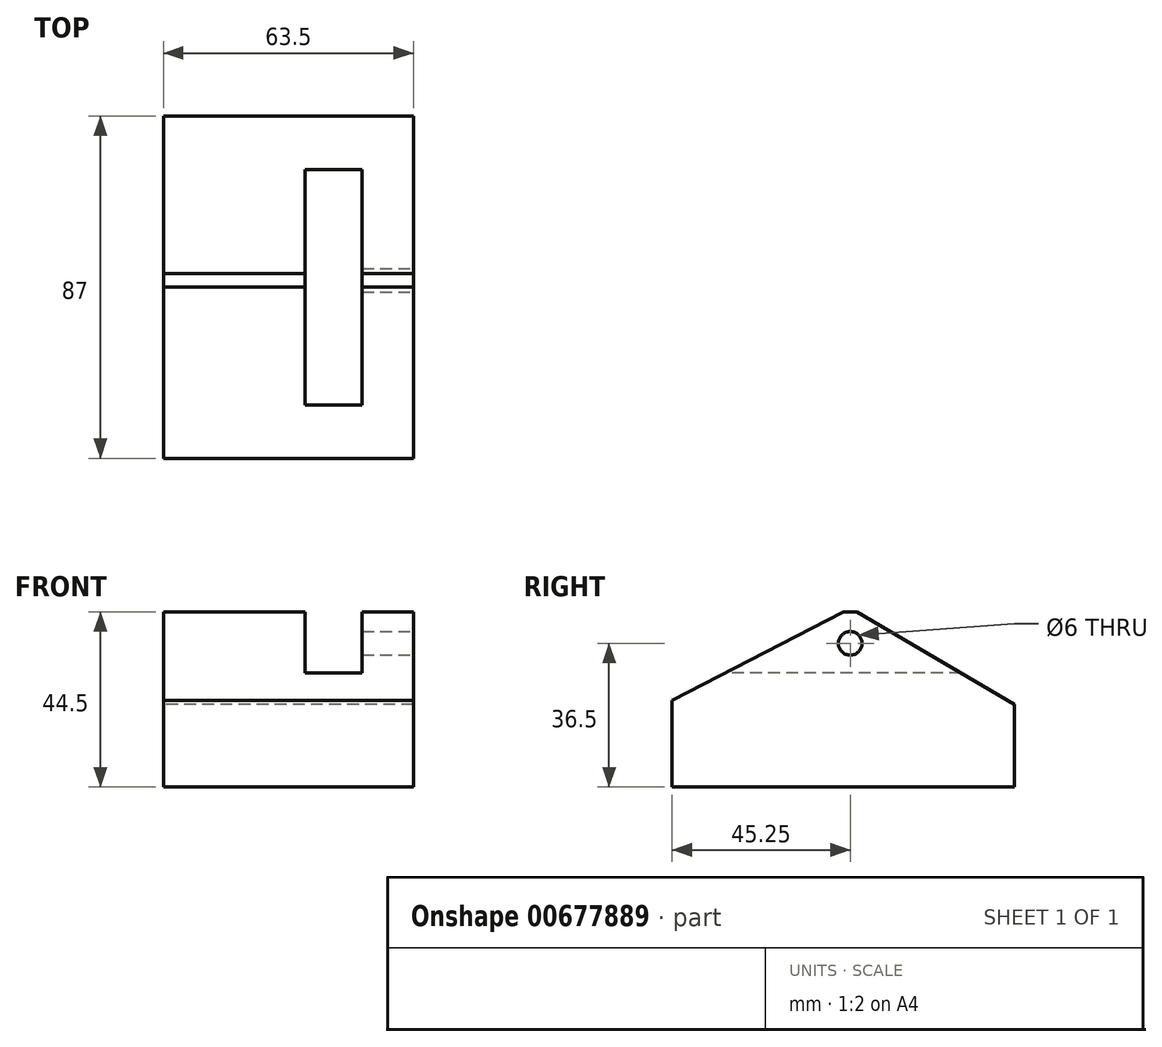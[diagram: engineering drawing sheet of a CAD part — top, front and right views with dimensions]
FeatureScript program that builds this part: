
annotation { "Feature Type Name" : "Feature", "Feature Type Description" : "" }
export const myFeature = defineFeature(function(context is Context, id is Id, definition is map)
    precondition{}
    {
        {
            var Q0;
            Q0=qCreatedBy(makeId("Right.planeOp"),FACE);
            var sketch = newSketch(context, id + "F0", { "sketchPlane" : qUnion([Q0])});
            skLineSegment(sketch, "E0", {"start": v(0, 0) * mm, "end": v(0, 22) * mm});
            skLineSegment(sketch, "E1", {"start": v(0, 22) * mm, "end": v(43.5, 44.5) * mm});
            skLineSegment(sketch, "E2", {"start": v(43.5, 44.5) * mm, "end": v(47, 44.5) * mm});
            skLineSegment(sketch, "E3", {"start": v(47, 44.5) * mm, "end": v(87, 21) * mm});
            skLineSegment(sketch, "E4", {"start": v(87, 21) * mm, "end": v(87, 0) * mm});
            skLineSegment(sketch, "E5", {"start": v(87, 0) * mm, "end": v(0, 0) * mm});
            skSolve(sketch);
        }
        {
            var Q0;
            Q0 = qSketchRegion(id + "F0", true);
            extrude(context, id + "F1", {"entities" : qUnion([Q0]), "depth" : 63.5 * mm, "offsetDistance" : 25 * mm});
        }
        {
            var Q0;
            Q0=makeQuery(id+"F1.opExtrude","SWEPT_FACE",FACE,{"disambiguationData":[OSD([sQuery(id+"F0.wireOp",EDGE,"E0")])]});
            var sketch = newSketch(context, id + "F2", { "sketchPlane" : qUnion([Q0])});
            skLineSegment(sketch, "E6.bottom", {"start": v(36, 52.93) * mm, "end": v(50.5, 52.93) * mm});
            skLineSegment(sketch, "E6.top", {"start": v(36, 29) * mm, "end": v(50.5, 29) * mm});
            skLineSegment(sketch, "E6.left", {"start": v(36, 52.93) * mm, "end": v(36, 29) * mm});
            skLineSegment(sketch, "E6.right", {"start": v(50.5, 52.93) * mm, "end": v(50.5, 29) * mm});
            skSolve(sketch);
        }
        {
            var Q0;
            Q0 = qSketchRegion(id + "F2", true);
            extrude(context, id + "F3", {"entities" : qUnion([Q0]), "operationType" : NewBodyOperationType.REMOVE, "oppositeDirection" : true, "depth" : 100 * mm, "offsetDistance" : 25 * mm});
        }
        {
            var Q0;
            Q0=makeQuery(id+"F1.opExtrude","CAP_FACE",FACE,{"disambiguationData":[OSD([sQuery(id+"F0.wireOp",EDGE,"E0"),sQuery(id+"F0.wireOp",EDGE,"E1"),sQuery(id+"F0.wireOp",EDGE,"E2"),sQuery(id+"F0.wireOp",EDGE,"E3"),sQuery(id+"F0.wireOp",EDGE,"E4"),sQuery(id+"F0.wireOp",EDGE,"E5")])],"isStart":false});
            var sketch = newSketch(context, id + "F4", { "sketchPlane" : qUnion([Q0])});
            skCircle(sketch, "E7", {"center": v(45.25, 36.5) * mm, "radius": 3 * mm});
            skSolve(sketch);
        }
        {
            var Q0;
            Q0 = qSketchRegion(id + "F4", true);
            extrude(context, id + "F5", {"entities" : qUnion([Q0]), "operationType" : NewBodyOperationType.REMOVE, "oppositeDirection" : true, "depth" : 25 * mm, "offsetDistance" : 25 * mm});
        }
    });
